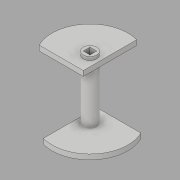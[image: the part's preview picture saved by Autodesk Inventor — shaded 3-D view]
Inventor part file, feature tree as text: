
AUTODESK INVENTOR PART (.ipt)
format: ipt  version: 2017 (Build 210142000, 142)  size: 113,664 bytes
history: native  units: mm
features: extrude x4, sketch x4, plane x1
ambient origin geometry x8: Origin, YZ Plane, XZ Plane, XY Plane, X Axis, Y Axis, Z Axis, Center Point
bodies: Solid1 (feature_tree), Solid2 (feature_tree)
feature tree (9):
  extrude  "Extrusion1"  Depth=4.0mm
  plane  "Work Plane5"
  extrude  "Extrusion4"  Depth=40.0mm TaperAngle=0.0deg
  extrude  "Extrusion5"  Depth=3.0mm TaperAngle=0.0deg
  extrude  "Extrusion3"  Depth=5.0mm
  sketch  "Sketch1"  dims[d0=40.0mm d1=0.0mm d5=4.0mm]
  sketch  "Sketch3"  dims[d6=4.0mm d7=40.0mm d8=0.0mm]
  sketch  "Sketch5"  dims[d13=3.0mm d14=0.0mm d15=3.0mm d16=0.0mm]
  sketch  "Sketch6"  dims[d17=5.0mm d18=0.0mm d19=45.0mm d20=45.0mm]
